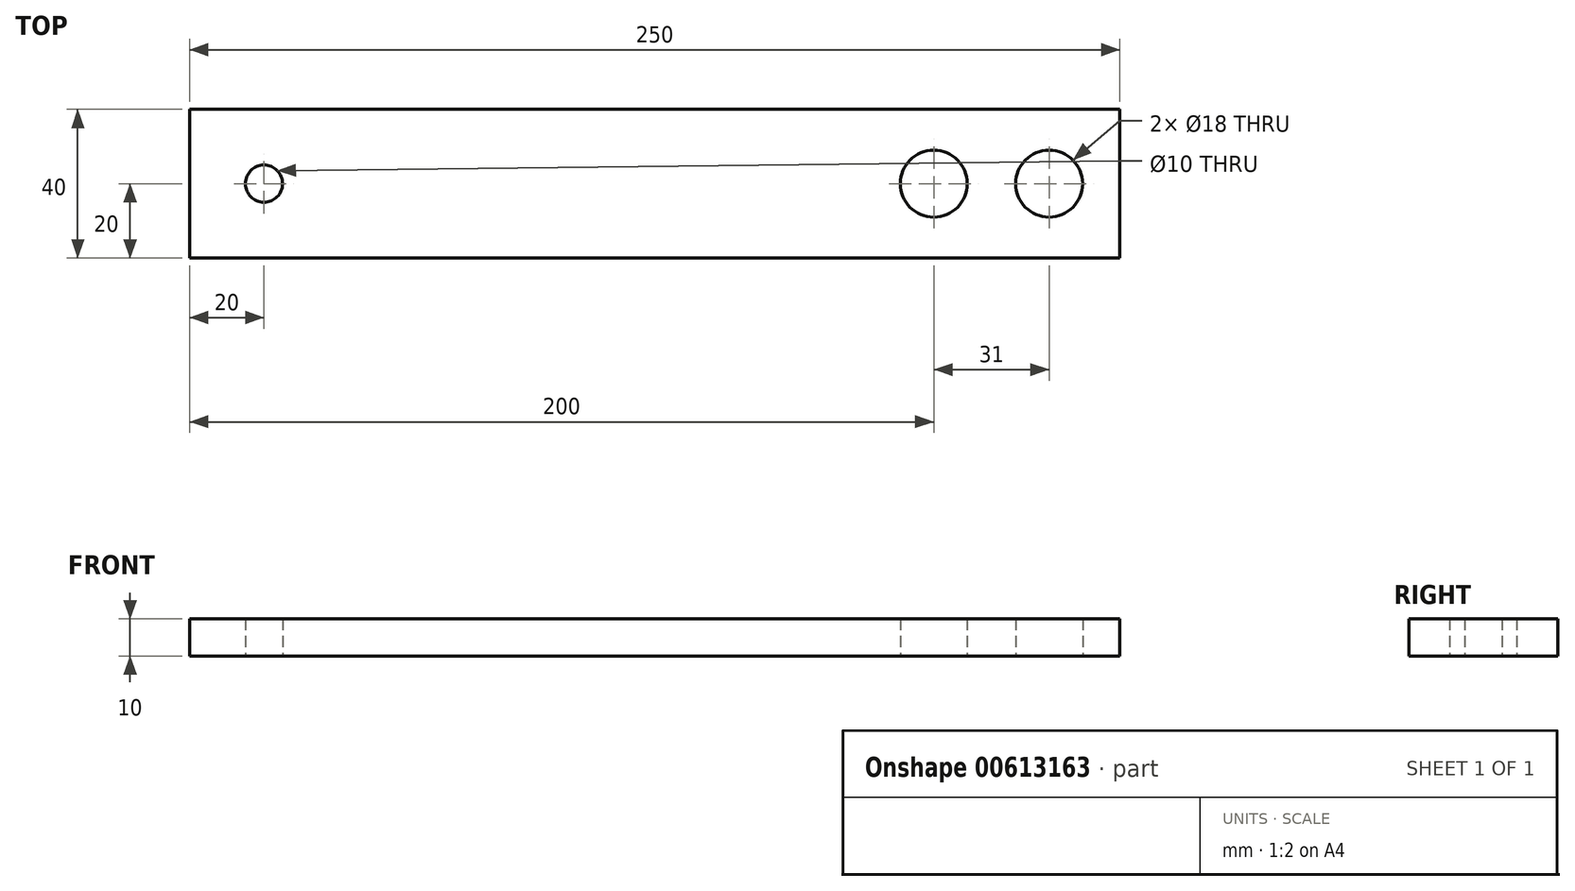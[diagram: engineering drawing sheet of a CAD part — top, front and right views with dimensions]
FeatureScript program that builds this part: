
annotation { "Feature Type Name" : "Feature", "Feature Type Description" : "" }
export const myFeature = defineFeature(function(context is Context, id is Id, definition is map)
    precondition{}
    {
        {
            var Q0;
            Q0=qCreatedBy(makeId("Top.planeOp"),FACE);
            var sketch = newSketch(context, id + "F0", { "sketchPlane" : qUnion([Q0])});
            skLineSegment(sketch, "E0.bottom", {"start": v(125, 20) * mm, "end": v(-125, 20) * mm});
            skLineSegment(sketch, "E0.top", {"start": v(125, -20) * mm, "end": v(-125, -20) * mm});
            skLineSegment(sketch, "E0.left", {"start": v(125, 20) * mm, "end": v(125, -20) * mm});
            skLineSegment(sketch, "E0.right", {"start": v(-125, 20) * mm, "end": v(-125, -20) * mm});
            skPoint(sketch, "E0.middle", {"position": v(0, 0) * mm});
            skCircle(sketch, "E1", {"center": v(-105, 0) * mm, "radius": 5 * mm});
            skSolve(sketch);
        }
        {
            var Q0;
            Q0=makeQuery(id+"F0.imprint","IMPRINT",FACE,{"disambiguationData":[TD([[makeQuery(id+"F0.imprint","IMPRINT",EDGE,{"derivedFrom":sQuery(id+"F0.wireOp",EDGE,"E0.bottom")}),1.0]])]});
            extrude(context, id + "F1", {"entities" : qUnion([Q0]), "depth" : 10 * mm, "offsetDistance" : 25 * mm});
        }
        {
            var Q0;
            Q0=makeQuery(id+"F1.opExtrude","CAP_FACE",FACE,{"disambiguationData":[OSD([sQuery(id+"F0.wireOp",EDGE,"E0.bottom"),sQuery(id+"F0.wireOp",EDGE,"E0.top"),sQuery(id+"F0.wireOp",EDGE,"E0.left"),sQuery(id+"F0.wireOp",EDGE,"E0.right"),sQuery(id+"F0.wireOp",EDGE,"E1")])],"isStart":true});
            var sketch = newSketch(context, id + "F2", { "sketchPlane" : qUnion([Q0])});
            skCircle(sketch, "E2", {"center": v(106, 0) * mm, "radius": 9 * mm});
            skSolve(sketch);
        }
        {
            var Q0;
            Q0=qSketchRegion(id+"F2",true);
            extrude(context, id + "F3", {"entities" : qUnion([Q0]), "operationType" : NewBodyOperationType.REMOVE, "oppositeDirection" : true, "depth" : 25 * mm, "offsetDistance" : 25 * mm});
        }
        {
            var Q0;
            Q0=makeQuery(id+"F1.opExtrude","CAP_FACE",FACE,{"disambiguationData":[OSD([sQuery(id+"F0.wireOp",EDGE,"E0.bottom"),sQuery(id+"F0.wireOp",EDGE,"E0.top"),sQuery(id+"F0.wireOp",EDGE,"E0.left"),sQuery(id+"F0.wireOp",EDGE,"E0.right"),sQuery(id+"F0.wireOp",EDGE,"E1")])],"isStart":true});
            var sketch = newSketch(context, id + "F4", { "sketchPlane" : qUnion([Q0])});
            skCircle(sketch, "E3", {"center": v(75, 0) * mm, "radius": 9 * mm});
            skSolve(sketch);
        }
        {
            var Q0;
            Q0 = qSketchRegion(id + "F4", true);
            extrude(context, id + "F5", {"entities" : qUnion([Q0]), "operationType" : NewBodyOperationType.REMOVE, "oppositeDirection" : true, "depth" : 25 * mm, "offsetDistance" : 25 * mm});
        }
    });
